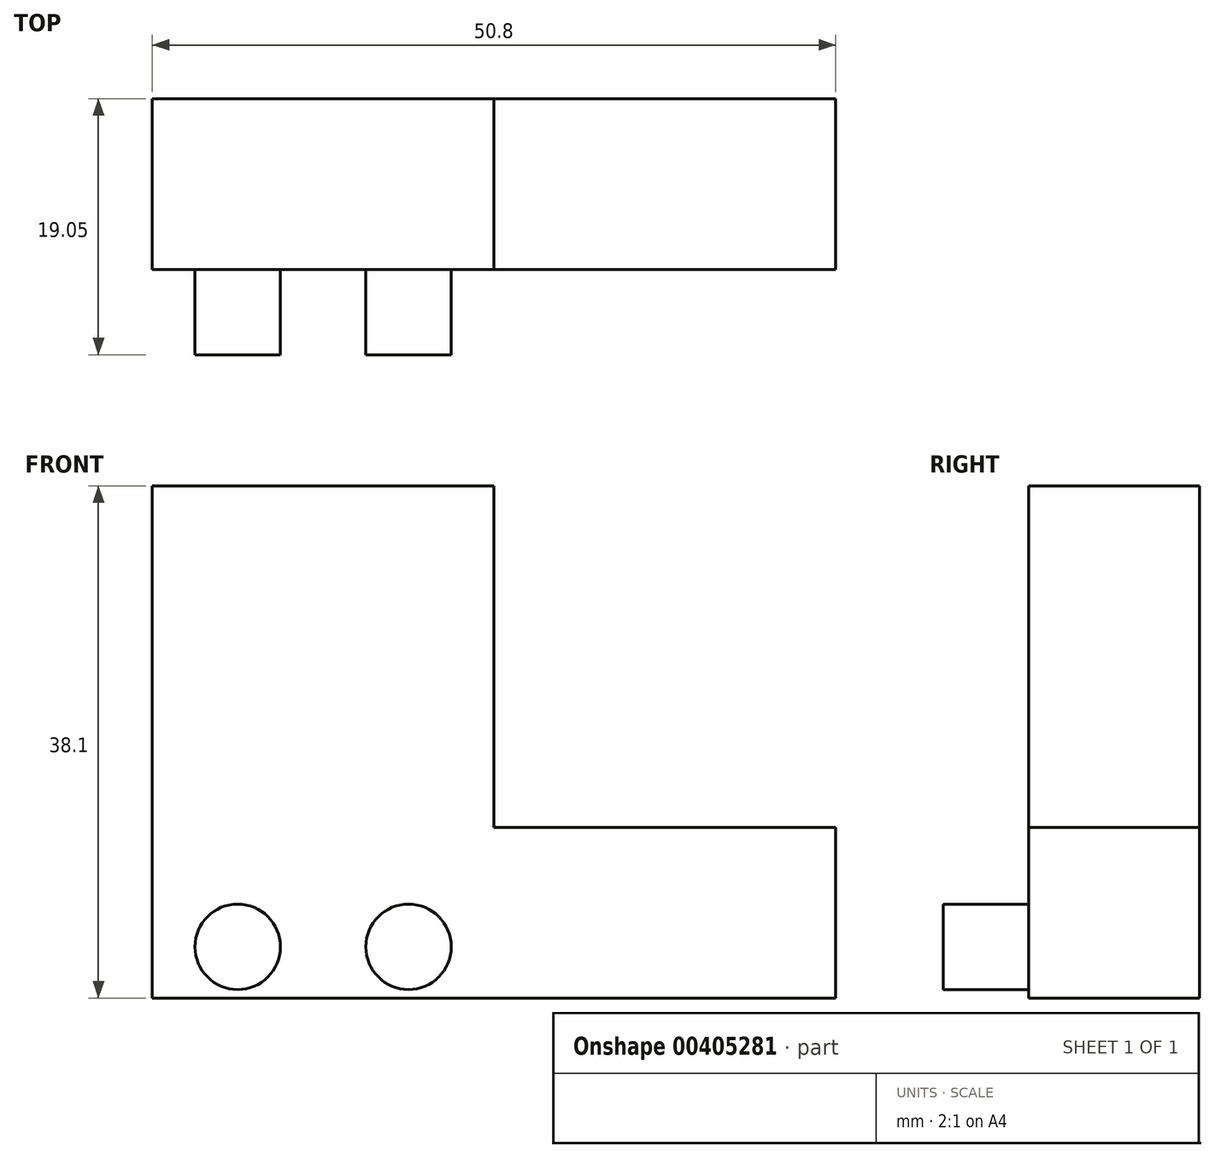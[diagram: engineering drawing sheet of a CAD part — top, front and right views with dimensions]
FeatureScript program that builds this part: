
annotation { "Feature Type Name" : "Feature", "Feature Type Description" : "" }
export const myFeature = defineFeature(function(context is Context, id is Id, definition is map)
    precondition{}
    {
        {
            var Q0;
            Q0=qCreatedBy(makeId("Front.planeOp"),FACE);
            var sketch = newSketch(context, id + "F0", { "sketchPlane" : qUnion([Q0])});
            skLineSegment(sketch, "E0", {"start": v(0, 0) * mm, "end": v(0, 12.7) * mm});
            skLineSegment(sketch, "E1", {"start": v(0, 0) * mm, "end": v(-50.8, 0) * mm});
            skLineSegment(sketch, "E2", {"start": v(0, 12.7) * mm, "end": v(-25.4, 12.7) * mm});
            skLineSegment(sketch, "E3", {"start": v(-25.4, 12.7) * mm, "end": v(-25.4, 38.1) * mm});
            skLineSegment(sketch, "E4", {"start": v(-25.4, 38.1) * mm, "end": v(-50.8, 38.1) * mm});
            skLineSegment(sketch, "E5", {"start": v(-50.8, 38.1) * mm, "end": v(-50.8, 0) * mm});
            skSolve(sketch);
        }
        {
            var Q0;
            Q0=makeQuery(id+"F0.imprint","IMPRINT",FACE,{"disambiguationData":[TD([[makeQuery(id+"F0.imprint","IMPRINT",EDGE,{"derivedFrom":sQuery(id+"F0.wireOp",EDGE,"E0")}),1.0]])]});
            extrude(context, id + "F1", {"entities" : qUnion([Q0]), "depth" : 12.7 * mm});
        }
        {
            var Q0;
            Q0=makeQuery(id+"F1.opExtrude","CAP_FACE",FACE,{"disambiguationData":[OSD([sQuery(id+"F0.wireOp",EDGE,"E0"),sQuery(id+"F0.wireOp",EDGE,"E1"),sQuery(id+"F0.wireOp",EDGE,"E2"),sQuery(id+"F0.wireOp",EDGE,"E3"),sQuery(id+"F0.wireOp",EDGE,"E4"),sQuery(id+"F0.wireOp",EDGE,"E5")])],"isStart":false});
            var sketch = newSketch(context, id + "F2", { "sketchPlane" : qUnion([Q0])});
            skCircle(sketch, "E6", {"center": v(-44.45, 3.81) * mm, "radius": 3.18 * mm});
            skCircle(sketch, "E7", {"center": v(-31.75, 3.81) * mm, "radius": 3.18 * mm});
            skLineSegment(sketch, "E8", {"start": v(-31.75, 3.81) * mm, "end": v(-44.45, 3.81) * mm});
            skSolve(sketch);
        }
        {
            var Q0;
            Q0 = qSketchRegion(id + "F2", true);
            extrude(context, id + "F3", {"entities" : qUnion([Q0]), "operationType" : NewBodyOperationType.ADD, "depth" : 6.35 * mm});
        }
    });
